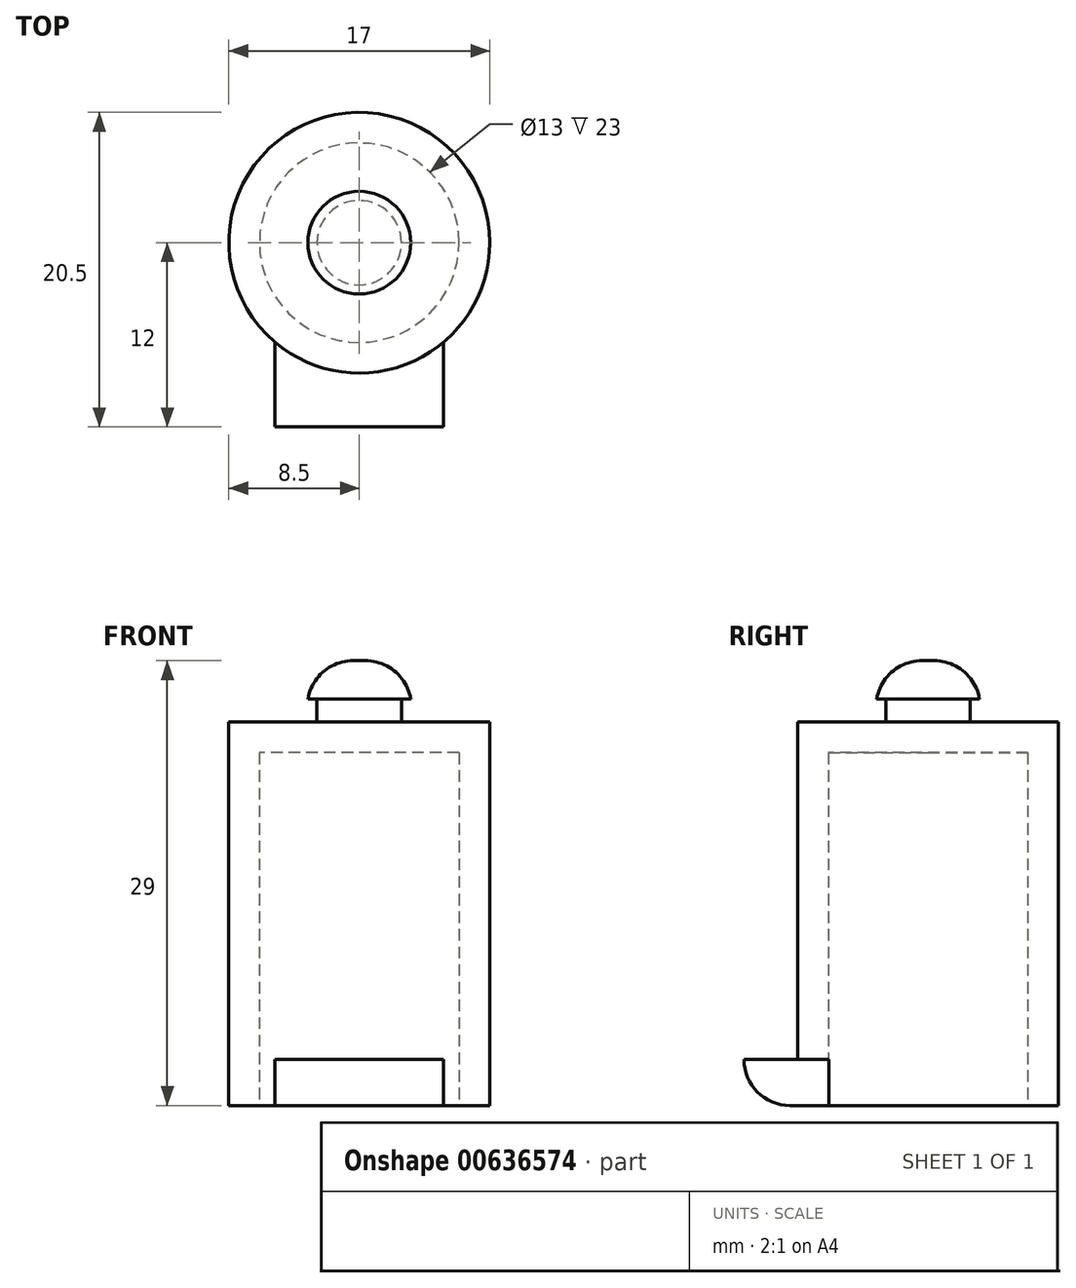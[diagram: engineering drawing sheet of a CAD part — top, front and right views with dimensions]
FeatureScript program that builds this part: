
annotation { "Feature Type Name" : "Feature", "Feature Type Description" : "" }
export const myFeature = defineFeature(function(context is Context, id is Id, definition is map)
    precondition{}
    {
        {
            var Q0;
            Q0=qCreatedBy(makeId("Top.planeOp"),FACE);
            var sketch = newSketch(context, id + "F0", { "sketchPlane" : qUnion([Q0])});
            skCircle(sketch, "E0", {"center": v(0, 0) * mm, "radius": 8.5 * mm});
            skCircle(sketch, "E1", {"center": v(0, 0) * mm, "radius": 6.5 * mm});
            skSolve(sketch);
        }
        {
            var Q0;
            Q0 = qSketchRegion(id + "F0", true);
            extrude(context, id + "F1", {"entities" : qUnion([Q0]), "depth" : 23 * mm, "offsetDistance" : 25 * mm});
        }
        {
            var Q0;
            Q0=makeQuery(id+"F1.opExtrude","CAP_FACE",FACE,{"disambiguationData":[OSD([sQuery(id+"F0.wireOp",EDGE,"E0"),sQuery(id+"F0.wireOp",EDGE,"E1")])],"isStart":false});
            var sketch = newSketch(context, id + "F2", { "sketchPlane" : qUnion([Q0])});
            skCircle(sketch, "E2.0", {"center": v(0, 0) * mm, "radius": 8.5 * mm});
            skSolve(sketch);
        }
        {
            var Q0;
            Q0 = qSketchRegion(id + "F2", true);
            extrude(context, id + "F3", {"entities" : qUnion([Q0]), "operationType" : NewBodyOperationType.ADD, "depth" : 2 * mm, "offsetDistance" : 25 * mm});
        }
        {
            var Q0;
            Q0=makeQuery(id+"F1.opExtrude","CAP_FACE",FACE,{"disambiguationData":[OSD([sQuery(id+"F0.wireOp",EDGE,"E0"),sQuery(id+"F0.wireOp",EDGE,"E1")])],"isStart":true});
            var sketch = newSketch(context, id + "F4", { "sketchPlane" : qUnion([Q0])});
            skLineSegment(sketch, "E3", {"start": v(0, 8.5) * mm, "end": v(0, 12) * mm});
            skLineSegment(sketch, "E4", {"start": v(0, 12) * mm, "end": v(5.5, 12) * mm});
            skArc(sketch, "E5.0", {"start": v(5.5, 6.48) * mm, "mid": v(0, 8.5) * mm, "end": v(-5.5, 6.48) * mm});
            skLineSegment(sketch, "E6", {"start": v(5.5, 12) * mm, "end": v(5.5, 6.48) * mm});
            skLineSegment(sketch, "E7.MirrorCS", {"start": v(0, 12) * mm, "end": v(-5.5, 12) * mm});
            skLineSegment(sketch, "E8.MirrorCS", {"start": v(-5.5, 12) * mm, "end": v(-5.5, 6.48) * mm});
            skSolve(sketch);
        }
        {
            var Q0;
            Q0 = qSketchRegion(id + "F4", true);
            extrude(context, id + "F5", {"entities" : qUnion([Q0]), "operationType" : NewBodyOperationType.ADD, "oppositeDirection" : true, "depth" : 3 * mm, "offsetDistance" : 25 * mm});
        }
        {
            var Q0;
            Q0=makeQuery(id+"F5.opExtrude","CAP_EDGE",EDGE,{"disambiguationData":[OSD([sQuery(id+"F4.wireOp",EDGE,"E4"),sQuery(id+"F4.wireOp",EDGE,"E7.MirrorCS")])],"isStart":true});
            fillet(context, id + "F6", {"entities" : qUnion([Q0]), "radius" : 3 * mm, "tangentPropagation" : true, "allowEdgeOverflow" : false});
        }
        {
            var Q0;
            Q0=makeQuery(id+"F3.opExtrude","CAP_FACE",FACE,{"disambiguationData":[OSD([sQuery(id+"F2.wireOp",EDGE,"E2.0")])],"isStart":false});
            var sketch = newSketch(context, id + "F7", { "sketchPlane" : qUnion([Q0])});
            skCircle(sketch, "E9", {"center": v(0, 0) * mm, "radius": 2.75 * mm});
            skSolve(sketch);
        }
        {
            var Q0;
            Q0 = qSketchRegion(id + "F7", true);
            extrude(context, id + "F8", {"entities" : qUnion([Q0]), "operationType" : NewBodyOperationType.ADD, "depth" : 1.5 * mm, "offsetDistance" : 25 * mm});
        }
        {
            var Q0;
            Q0=makeQuery(id+"F8.opExtrude","CAP_FACE",FACE,{"disambiguationData":[OSD([sQuery(id+"F7.wireOp",EDGE,"E9")])],"isStart":false});
            var sketch = newSketch(context, id + "F9", { "sketchPlane" : qUnion([Q0])});
            skCircle(sketch, "E10", {"center": v(0, 0) * mm, "radius": 3.35 * mm});
            skSolve(sketch);
        }
        {
            var Q0;
            Q0 = qSketchRegion(id + "F9", true);
            extrude(context, id + "F10", {"entities" : qUnion([Q0]), "operationType" : NewBodyOperationType.ADD, "depth" : 2.5 * mm, "offsetDistance" : 25 * mm});
        }
        {
            var Q0;
            Q0=makeQuery(id+"F10.opExtrude","CAP_EDGE",EDGE,{"disambiguationData":[OSD([sQuery(id+"F9.wireOp",EDGE,"E10")])],"isStart":false});
            fillet(context, id + "F11", {"entities" : qUnion([Q0]), "radius" : 3 * mm, "tangentPropagation" : true, "allowEdgeOverflow" : false});
        }
    });
